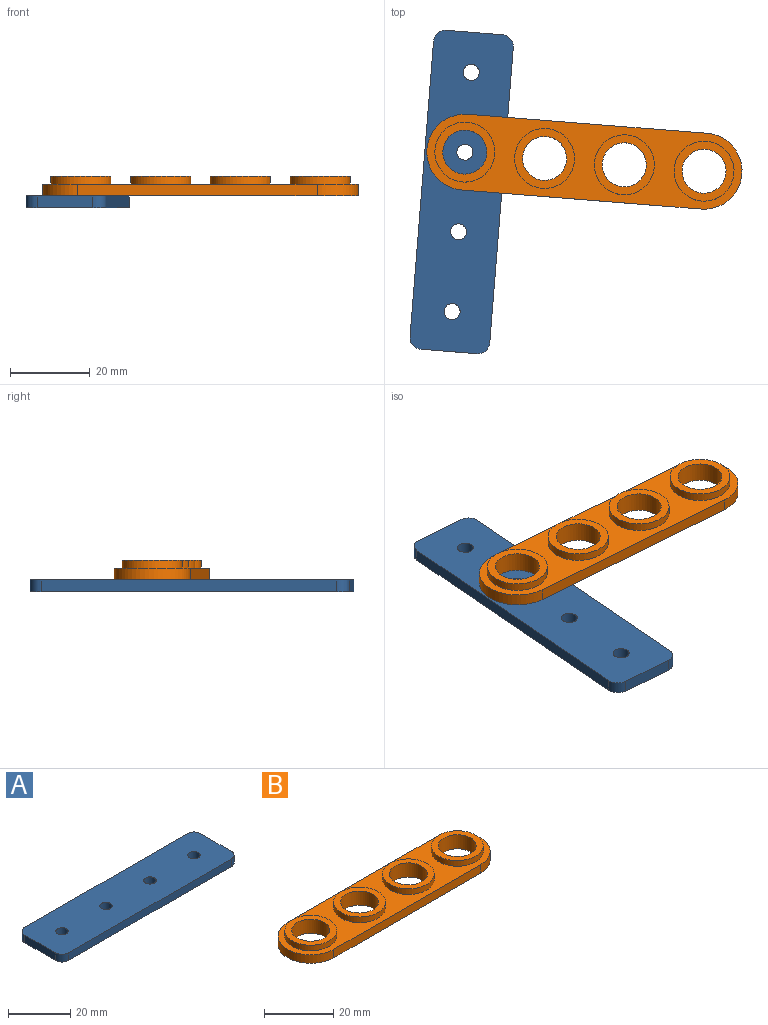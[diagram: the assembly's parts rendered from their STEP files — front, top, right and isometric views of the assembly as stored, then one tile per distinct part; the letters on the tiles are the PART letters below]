
ASSEMBLY  parts=2 mates=2
PART A: 14 faces, bbox 80x20x3 mm
  f0: plane 74x3mm, normal (0,-1,0), area 222mm2, adj f1,f11,f12,f13
  f1: cylinder r=3mm len=3mm, axis (0,0,-1), area 14.1mm2, adj f0,f2,f12,f13
  f2: plane 14x3mm, normal (1,0,0), area 42mm2, adj f1,f3,f12,f13
  f3: cylinder r=3mm len=3mm, axis (0,0,-1), area 14.1mm2, adj f2,f4,f12,f13
  f4: plane 74x3mm, normal (0,1,0), area 222mm2, adj f3,f5,f12,f13
  f5: cylinder r=3mm len=3mm, axis (0,0,-1), area 14.1mm2, adj f4,f6,f12,f13
  f6: plane 14x3mm, normal (-1,0,0), area 42mm2, adj f5,f11,f12,f13
  f7: cylinder r=2mm len=4mm, axis (0,0,-1), area 37.7mm2, adj f12,f13
  f8: cylinder r=2mm len=4mm, axis (0,0,-1), area 37.7mm2, adj f12,f13
  f9: cylinder r=2mm len=4mm, axis (0,0,-1), area 37.7mm2, adj f12,f13
  f10: cylinder r=2mm len=4mm, axis (0,0,-1), area 37.7mm2, adj f12,f13
  f11: cylinder r=3mm len=3mm, axis (0,0,-1), area 14.1mm2, adj f0,f6,f12,f13
  f12: plane 80x20mm, normal (0,0,1), area 1542mm2, adj f0,f1,f2,f3,f4,f5,f6,f7
  f13: plane 80x20mm, normal (0,0,-1), area 1542mm2, adj f0,f1,f2,f3,f4,f5,f6,f7
PART B: 18 faces, bbox 79x19x5 mm
  f0: cylinder r=5.5mm len=11mm, axis (0,0,-1), area 172.8mm2, adj f2,f3
  f1: cylinder r=7.5mm len=15mm, axis (0,0,-1), area 94.2mm2, adj f2,f17
  f2: plane 15x15mm, normal (0,0,1), area 81.7mm2, adj f0,f1
  f3: plane 79x19mm, normal (0,0,-1), area 1043.4mm2, adj f0,f4,f7,f10,f13,f14,f15,f16
  f4: cylinder r=5.5mm len=11mm, axis (0,0,-1), area 172.8mm2, adj f3,f6
  f5: cylinder r=7.5mm len=15mm, axis (0,0,-1), area 94.2mm2, adj f6,f17
  f6: plane 15x15mm, normal (0,0,1), area 81.7mm2, adj f4,f5
  f7: cylinder r=5.5mm len=11mm, axis (0,0,-1), area 172.8mm2, adj f3,f9
  f8: cylinder r=7.5mm len=15mm, axis (0,0,-1), area 94.2mm2, adj f9,f17
  f9: plane 15x15mm, normal (0,0,1), area 81.7mm2, adj f7,f8
  f10: cylinder r=5.5mm len=11mm, axis (0,0,-1), area 172.8mm2, adj f3,f12
  f11: cylinder r=7.5mm len=15mm, axis (0,0,-1), area 94.2mm2, adj f12,f17
  f12: plane 15x15mm, normal (0,0,1), area 81.7mm2, adj f10,f11
  f13: plane 60x3mm, normal (0,1,0), area 180mm2, adj f3,f14,f16,f17
  f14: cylinder r=9.5mm len=19mm, axis (0,0,-1), area 89.5mm2, adj f3,f13,f15,f17
  f15: plane 60x3mm, normal (0,-1,0), area 180mm2, adj f3,f14,f16,f17
  f16: cylinder r=9.5mm len=19mm, axis (0,0,-1), area 89.5mm2, adj f3,f13,f15,f17
  f17: plane 79x19mm, normal (0,0,1), area 716.7mm2, adj f1,f5,f8,f11,f13,f14,f15,f16
PLACE A rot(axis=(0,0,-1),94.6deg) t=(-44.47,-27.85,-15.06)mm
PLACE B rot(axis=(0,0,-1),4.6deg) t=(-43.68,-17.88,-12.06)mm
MATE planar A.f10 <-> B.f3  axis (0,0,1) through (-42.09,2.05,-12.06)mm
MATE revolute B.f0 <-> A.f9  axis (0,0,-1) through (-43.68,-17.88,-12.06)mm
